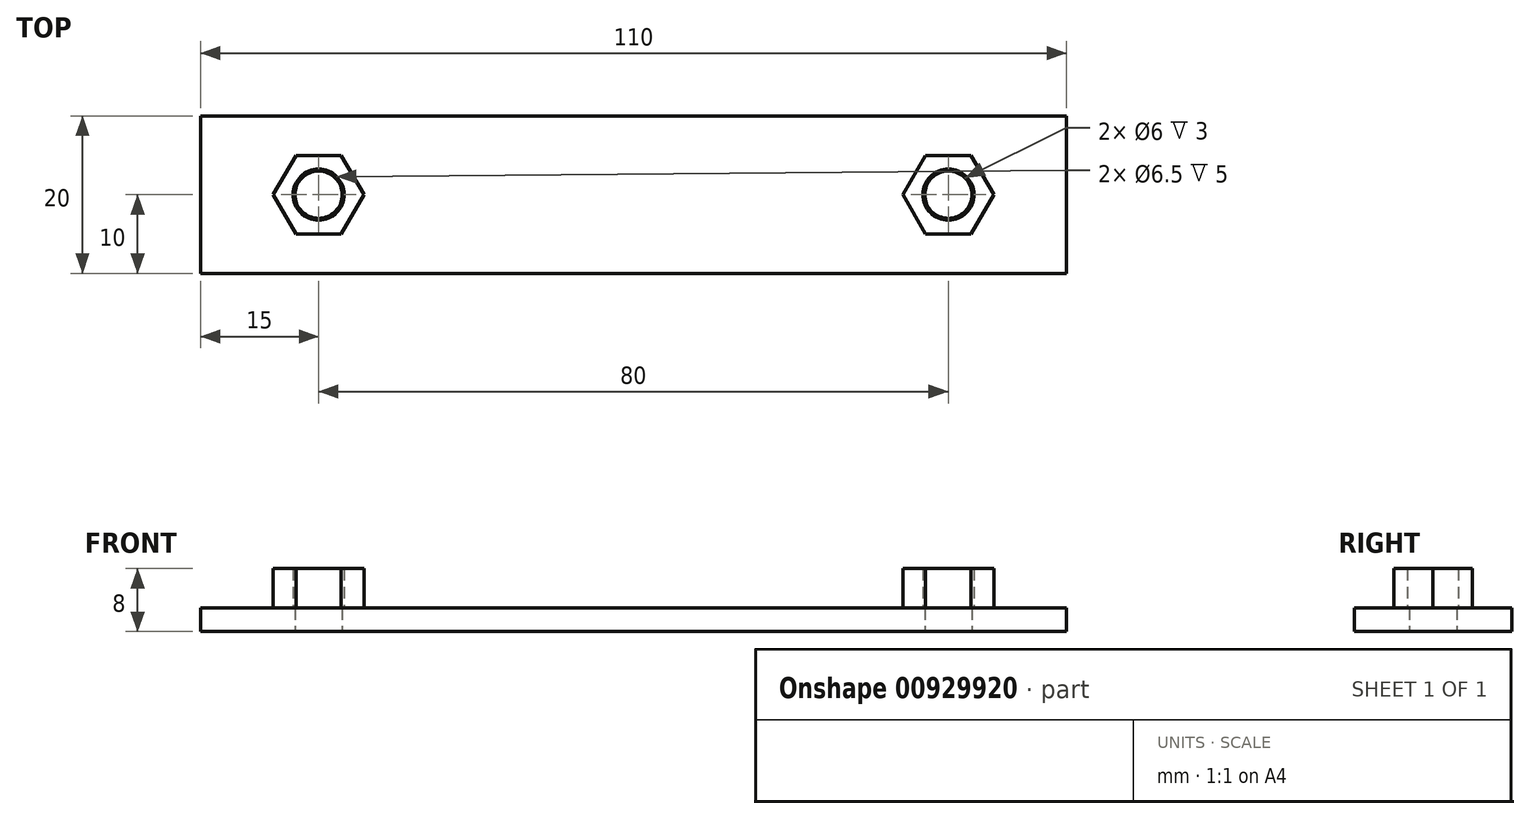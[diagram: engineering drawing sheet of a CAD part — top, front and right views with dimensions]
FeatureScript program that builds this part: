
annotation { "Feature Type Name" : "Feature", "Feature Type Description" : "" }
export const myFeature = defineFeature(function(context is Context, id is Id, definition is map)
    precondition{}
    {
        {
            var Q0;
            Q0=qCreatedBy(makeId("Top.planeOp"),FACE);
            var sketch = newSketch(context, id + "F0", { "sketchPlane" : qUnion([Q0])});
            skLineSegment(sketch, "E0.bottom", {"start": v(0, 0) * mm, "end": v(110, 0) * mm});
            skLineSegment(sketch, "E0.top", {"start": v(0, 20) * mm, "end": v(110, 20) * mm});
            skLineSegment(sketch, "E0.left", {"start": v(0, 0) * mm, "end": v(0, 20) * mm});
            skLineSegment(sketch, "E0.right", {"start": v(110, 0) * mm, "end": v(110, 20) * mm});
            skCircle(sketch, "E1", {"center": v(15, 10) * mm, "radius": 3 * mm});
            skCircle(sketch, "E2", {"center": v(95, 10) * mm, "radius": 3 * mm});
            skSolve(sketch);
        }
        {
            var Q0;
            Q0 = qSketchRegion(id + "F0", true);
            extrude(context, id + "F1", {"entities" : qUnion([Q0]), "depth" : 3 * mm, "offsetDistance" : 25 * mm});
        }
        {
            var Q0;
            Q0=makeQuery(id+"F1.opExtrude","CAP_FACE",FACE,{"disambiguationData":[OSD([sQuery(id+"F0.wireOp",EDGE,"E0.bottom"),sQuery(id+"F0.wireOp",EDGE,"E0.top"),sQuery(id+"F0.wireOp",EDGE,"E0.left"),sQuery(id+"F0.wireOp",EDGE,"E0.right"),sQuery(id+"F0.wireOp",EDGE,"E1"),sQuery(id+"F0.wireOp",EDGE,"E2")])],"isStart":false});
            var sketch = newSketch(context, id + "F2", { "sketchPlane" : qUnion([Q0])});
            skCircle(sketch, "E3.cCircle", {"center": v(15, 10) * mm, "radius": 5 * mm, "construction": true});
            skLineSegment(sketch, "E3.0", {"start": v(20.77, 10) * mm, "end": v(17.89, 5) * mm});
            skLineSegment(sketch, "E3.1", {"start": v(17.89, 5) * mm, "end": v(12.11, 5) * mm});
            skLineSegment(sketch, "E3.2", {"start": v(12.11, 5) * mm, "end": v(9.23, 10) * mm});
            skLineSegment(sketch, "E3.3", {"start": v(9.23, 10) * mm, "end": v(12.11, 15) * mm});
            skLineSegment(sketch, "E3.4", {"start": v(12.11, 15) * mm, "end": v(17.89, 15) * mm});
            skLineSegment(sketch, "E3.5", {"start": v(17.89, 15) * mm, "end": v(20.77, 10) * mm});
            skPoint(sketch, "E3.0.midPoint", {"position": v(19.33, 7.5) * mm});
            skCircle(sketch, "E4", {"center": v(15, 10) * mm, "radius": 3.25 * mm});
            skCircle(sketch, "E5.cCircle", {"center": v(95, 10) * mm, "radius": 5 * mm, "construction": true});
            skLineSegment(sketch, "E5.0", {"start": v(100.77, 10) * mm, "end": v(97.89, 5) * mm});
            skLineSegment(sketch, "E5.1", {"start": v(97.89, 5) * mm, "end": v(92.11, 5) * mm});
            skLineSegment(sketch, "E5.2", {"start": v(92.11, 5) * mm, "end": v(89.23, 10) * mm});
            skLineSegment(sketch, "E5.3", {"start": v(89.23, 10) * mm, "end": v(92.11, 15) * mm});
            skLineSegment(sketch, "E5.4", {"start": v(92.11, 15) * mm, "end": v(97.89, 15) * mm});
            skLineSegment(sketch, "E5.5", {"start": v(97.89, 15) * mm, "end": v(100.77, 10) * mm});
            skPoint(sketch, "E5.0.midPoint", {"position": v(99.33, 7.5) * mm});
            skCircle(sketch, "E6", {"center": v(95, 10) * mm, "radius": 3.25 * mm});
            skSolve(sketch);
        }
        {
            var Q0;
            Q0 = qSketchRegion(id + "F2", true);
            extrude(context, id + "F3", {"entities" : qUnion([Q0]), "operationType" : NewBodyOperationType.ADD, "depth" : 5 * mm, "offsetDistance" : 25 * mm});
        }
    });
